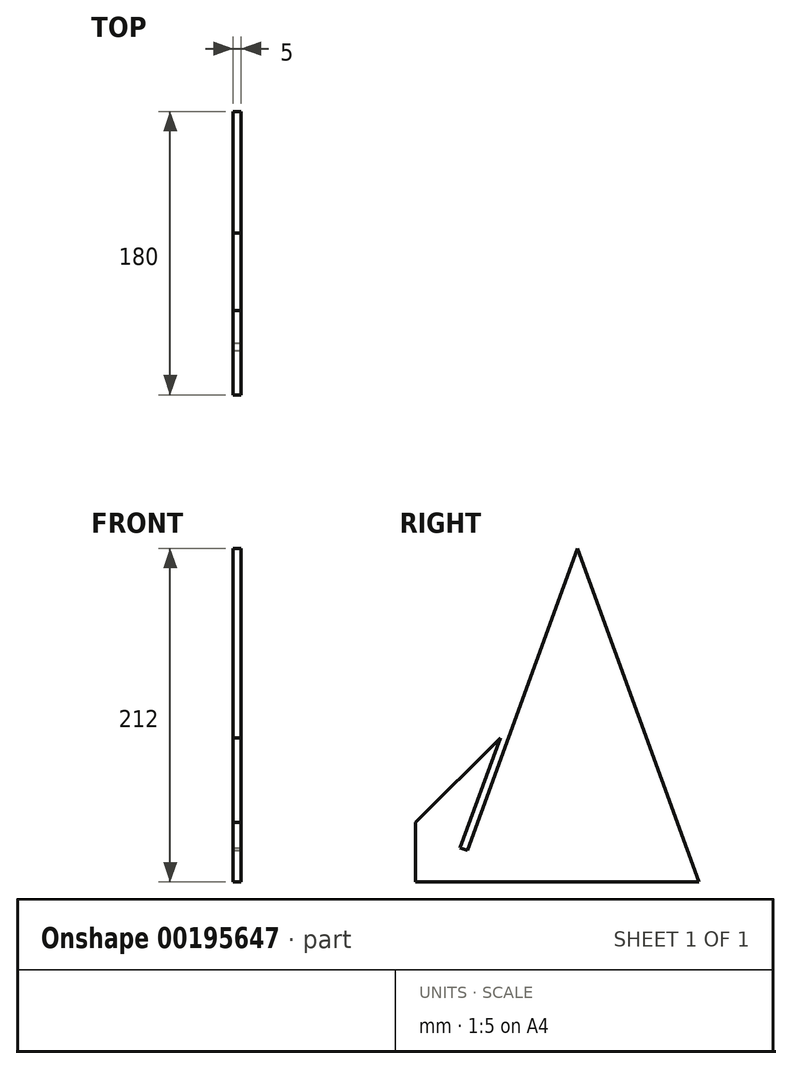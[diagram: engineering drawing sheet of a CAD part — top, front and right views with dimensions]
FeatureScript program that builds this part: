
annotation { "Feature Type Name" : "Feature", "Feature Type Description" : "" }
export const myFeature = defineFeature(function(context is Context, id is Id, definition is map)
    precondition{}
    {
        {
            var Q0;
            Q0=qCreatedBy(makeId("Right.planeOp"),FACE);
            var sketch = newSketch(context, id + "F0", { "sketchPlane" : qUnion([Q0])});
            skLineSegment(sketch, "E0", {"start": v(-90, 0) * mm, "end": v(90, 0) * mm});
            skLineSegment(sketch, "E1", {"start": v(-90, 37.93) * mm, "end": v(-36.3, 91.63) * mm});
            skLineSegment(sketch, "E2", {"start": v(12.84, 212) * mm, "end": v(90, 0) * mm});
            skLineSegment(sketch, "E3", {"start": v(12.84, 212) * mm, "end": v(-27.93, 100) * mm});
            skLineSegment(sketch, "E4", {"start": v(-27.93, 100) * mm, "end": v(-57.04, 20) * mm});
            skLineSegment(sketch, "E5", {"start": v(-57.04, 20) * mm, "end": v(-61.74, 21.71) * mm});
            skLineSegment(sketch, "E6", {"start": v(-61.74, 21.71) * mm, "end": v(-36.3, 91.63) * mm});
            skLineSegment(sketch, "E7", {"start": v(-90, 0) * mm, "end": v(-90, 37.93) * mm});
            skSolve(sketch);
        }
        {
            var Q0;
            Q0 = qSketchRegion(id + "F0", true);
            extrude(context, id + "F1", {"entities" : qUnion([Q0]), "oppositeDirection" : true, "depth" : 5 * mm});
        }
    });
